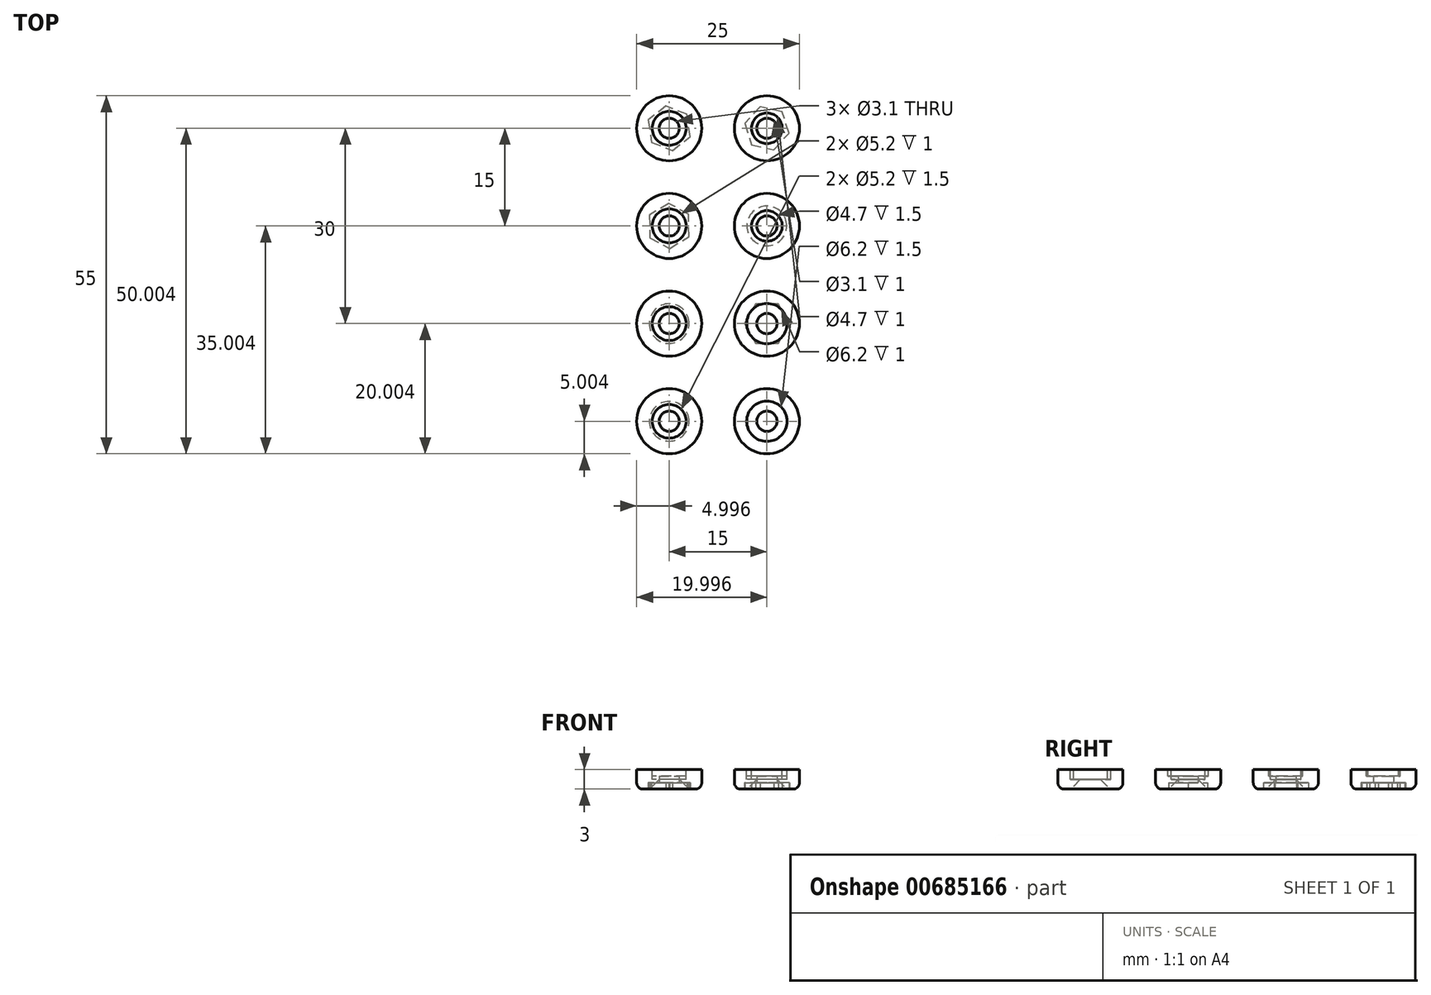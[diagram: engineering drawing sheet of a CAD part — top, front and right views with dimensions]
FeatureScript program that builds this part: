
annotation { "Feature Type Name" : "Feature", "Feature Type Description" : "" }
export const myFeature = defineFeature(function(context is Context, id is Id, definition is map)
    precondition{}
    {
        {
            var Q0;
            Q0=qCreatedBy(makeId("Top.planeOp"),FACE);
            var sketch = newSketch(context, id + "F0", { "sketchPlane" : qUnion([Q0])});
            skCircle(sketch, "E0", {"center": v(-31.01, -17.67) * mm, "radius": 5 * mm});
            skCircle(sketch, "E1.0.1.0", {"center": v(-31.01, -2.67) * mm, "radius": 5 * mm});
            skCircle(sketch, "E1.0.2.0", {"center": v(-31.01, 12.33) * mm, "radius": 5 * mm});
            skCircle(sketch, "E1.0.3.0", {"center": v(-31.01, 27.33) * mm, "radius": 5 * mm});
            skCircle(sketch, "E1.1.0.0", {"center": v(-16.01, -17.67) * mm, "radius": 5 * mm});
            skCircle(sketch, "E1.1.1.0", {"center": v(-16.01, -2.67) * mm, "radius": 5 * mm});
            skCircle(sketch, "E1.1.2.0", {"center": v(-16.01, 12.33) * mm, "radius": 5 * mm});
            skCircle(sketch, "E1.1.3.0", {"center": v(-16.01, 27.33) * mm, "radius": 5 * mm});
            skLineSegment(sketch, "E1.direction1", {"start": v(-31.01, -17.67) * mm, "end": v(-16.01, -17.67) * mm, "construction": true});
            skLineSegment(sketch, "E1.direction2", {"start": v(-31.01, -17.67) * mm, "end": v(-31.01, -2.67) * mm, "construction": true});
            skCircle(sketch, "E2", {"center": v(-31.01, -17.67) * mm, "radius": 1.55 * mm});
            skCircle(sketch, "E3", {"center": v(-16.01, -17.67) * mm, "radius": 1.55 * mm});
            skCircle(sketch, "E4", {"center": v(-31.01, -2.67) * mm, "radius": 1.55 * mm});
            skCircle(sketch, "E5", {"center": v(-16.01, -2.67) * mm, "radius": 1.55 * mm});
            skCircle(sketch, "E6", {"center": v(-31.01, 12.33) * mm, "radius": 1.55 * mm});
            skCircle(sketch, "E7", {"center": v(-31.01, 27.33) * mm, "radius": 1.55 * mm});
            skCircle(sketch, "E8", {"center": v(-16.01, 12.33) * mm, "radius": 1.55 * mm});
            skCircle(sketch, "E9", {"center": v(-16.01, 27.33) * mm, "radius": 1.55 * mm});
            skSolve(sketch);
        }
        {
            var Q0;
            Q0 = qSketchRegion(id + "F0", true);
            extrude(context, id + "F1", {"entities" : qUnion([Q0]), "depth" : 3 * mm, "offsetDistance" : 25 * mm});
        }
        {
            var Q0;
            Q0=makeQuery(id+"F1.opExtrude","CAP_FACE",FACE,{"disambiguationData":[OSD([sQuery(id+"F0.wireOp",EDGE,"E0")])],"isStart":false});
            var sketch = newSketch(context, id + "F2", { "sketchPlane" : qUnion([Q0])});
            skCircle(sketch, "E10", {"center": v(-31.01, -17.67) * mm, "radius": 2.6 * mm});
            skSolve(sketch);
        }
        {
            var Q0;
            Q0 = qSketchRegion(id + "F2", true);
            extrude(context, id + "F3", {"entities" : qUnion([Q0]), "operationType" : NewBodyOperationType.REMOVE, "oppositeDirection" : true, "depth" : 1.5 * mm, "offsetDistance" : 25 * mm});
        }
        {
            var Q0;
            Q0=makeQuery(id+"F1.opExtrude","CAP_FACE",FACE,{"disambiguationData":[OSD([sQuery(id+"F0.wireOp",EDGE,"E1.0.1.0")])],"isStart":false});
            var sketch = newSketch(context, id + "F4", { "sketchPlane" : qUnion([Q0])});
            skCircle(sketch, "E11", {"center": v(-31.01, -2.67) * mm, "radius": 2.6 * mm});
            skSolve(sketch);
        }
        {
            var Q0;
            Q0 = qSketchRegion(id + "F4", true);
            extrude(context, id + "F5", {"entities" : qUnion([Q0]), "operationType" : NewBodyOperationType.REMOVE, "oppositeDirection" : true, "depth" : 1.5 * mm, "offsetDistance" : 25 * mm});
        }
        {
            var Q0;
            Q0=makeQuery(id+"F1.opExtrude","CAP_FACE",FACE,{"disambiguationData":[OSD([sQuery(id+"F0.wireOp",EDGE,"E1.0.2.0")])],"isStart":false});
            var sketch = newSketch(context, id + "F6", { "sketchPlane" : qUnion([Q0])});
            skCircle(sketch, "E12", {"center": v(-31.01, 12.33) * mm, "radius": 2.6 * mm});
            skSolve(sketch);
        }
        {
            var Q0;
            Q0 = qSketchRegion(id + "F6", true);
            extrude(context, id + "F7", {"entities" : qUnion([Q0]), "operationType" : NewBodyOperationType.REMOVE, "oppositeDirection" : true, "depth" : 1 * mm, "offsetDistance" : 25 * mm});
        }
        {
            var Q0;
            Q0=makeQuery(id+"F1.opExtrude","CAP_FACE",FACE,{"disambiguationData":[OSD([sQuery(id+"F0.wireOp",EDGE,"E1.0.3.0")])],"isStart":false});
            var sketch = newSketch(context, id + "F8", { "sketchPlane" : qUnion([Q0])});
            skCircle(sketch, "E13", {"center": v(-31.01, 27.33) * mm, "radius": 2.6 * mm});
            skSolve(sketch);
        }
        {
            var Q0;
            Q0 = qSketchRegion(id + "F8", true);
            extrude(context, id + "F9", {"entities" : qUnion([Q0]), "operationType" : NewBodyOperationType.REMOVE, "oppositeDirection" : true, "depth" : 1 * mm, "offsetDistance" : 25 * mm});
        }
        {
            var Q0;
            Q0=makeQuery(id+"F1.opExtrude","CAP_FACE",FACE,{"disambiguationData":[OSD([sQuery(id+"F0.wireOp",EDGE,"E1.1.0.0")])],"isStart":false});
            var sketch = newSketch(context, id + "F10", { "sketchPlane" : qUnion([Q0])});
            skCircle(sketch, "E14", {"center": v(-16.01, -17.67) * mm, "radius": 3.1 * mm});
            skSolve(sketch);
        }
        {
            var Q0;
            Q0 = qSketchRegion(id + "F10", true);
            extrude(context, id + "F11", {"entities" : qUnion([Q0]), "operationType" : NewBodyOperationType.REMOVE, "oppositeDirection" : true, "depth" : 1.5 * mm, "offsetDistance" : 25 * mm});
        }
        {
            var Q0;
            Q0=makeQuery(id+"F1.opExtrude","CAP_FACE",FACE,{"disambiguationData":[OSD([sQuery(id+"F0.wireOp",EDGE,"E1.1.1.0")])],"isStart":false});
            var sketch = newSketch(context, id + "F12", { "sketchPlane" : qUnion([Q0])});
            skCircle(sketch, "E15", {"center": v(-16.01, -2.67) * mm, "radius": 3.1 * mm});
            skSolve(sketch);
        }
        {
            var Q0;
            Q0 = qSketchRegion(id + "F12", true);
            extrude(context, id + "F13", {"entities" : qUnion([Q0]), "operationType" : NewBodyOperationType.REMOVE, "oppositeDirection" : true, "depth" : 1 * mm, "offsetDistance" : 25 * mm});
        }
        {
            var Q0;
            Q0=makeQuery(id+"F1.opExtrude","CAP_FACE",FACE,{"disambiguationData":[OSD([sQuery(id+"F0.wireOp",EDGE,"E1.1.2.0")])],"isStart":false});
            var sketch = newSketch(context, id + "F14", { "sketchPlane" : qUnion([Q0])});
            skCircle(sketch, "E16", {"center": v(-16.01, 12.33) * mm, "radius": 2.35 * mm});
            skSolve(sketch);
        }
        {
            var Q0;
            Q0 = qSketchRegion(id + "F14", true);
            extrude(context, id + "F15", {"entities" : qUnion([Q0]), "operationType" : NewBodyOperationType.REMOVE, "oppositeDirection" : true, "depth" : 1.5 * mm, "offsetDistance" : 25 * mm});
        }
        {
            var Q0;
            Q0=makeQuery(id+"F1.opExtrude","CAP_FACE",FACE,{"disambiguationData":[OSD([sQuery(id+"F0.wireOp",EDGE,"E1.1.3.0")])],"isStart":false});
            var sketch = newSketch(context, id + "F16", { "sketchPlane" : qUnion([Q0])});
            skCircle(sketch, "E17", {"center": v(-16.01, 27.33) * mm, "radius": 2.35 * mm});
            skSolve(sketch);
        }
        {
            var Q0;
            Q0 = qSketchRegion(id + "F16", true);
            extrude(context, id + "F17", {"entities" : qUnion([Q0]), "operationType" : NewBodyOperationType.REMOVE, "oppositeDirection" : true, "depth" : 1 * mm, "offsetDistance" : 25 * mm});
        }
        {
            var Q0;
            Q0=makeQuery(id+"F1.opExtrude","CAP_FACE",FACE,{"disambiguationData":[OSD([sQuery(id+"F0.wireOp",EDGE,"E1.0.3.0")])],"isStart":true});
            var sketch = newSketch(context, id + "F18", { "sketchPlane" : qUnion([Q0])});
            skCircle(sketch, "E18.cCircle", {"center": v(-31.01, -27.33) * mm, "radius": 3 * mm, "construction": true});
            skLineSegment(sketch, "E18.0", {"start": v(-28.29, -29.47) * mm, "end": v(-31.5, -30.76) * mm});
            skLineSegment(sketch, "E18.1", {"start": v(-31.5, -30.76) * mm, "end": v(-34.23, -28.62) * mm});
            skLineSegment(sketch, "E18.2", {"start": v(-34.23, -28.62) * mm, "end": v(-33.74, -25.2) * mm});
            skLineSegment(sketch, "E18.3", {"start": v(-33.74, -25.2) * mm, "end": v(-30.52, -23.9) * mm});
            skLineSegment(sketch, "E18.4", {"start": v(-30.52, -23.9) * mm, "end": v(-27.8, -26.04) * mm});
            skLineSegment(sketch, "E18.5", {"start": v(-27.8, -26.04) * mm, "end": v(-28.29, -29.47) * mm});
            skPoint(sketch, "E18.0.midPoint", {"position": v(-29.9, -30.12) * mm});
            skSolve(sketch);
        }
        {
            var Q0;
            Q0 = qSketchRegion(id + "F18", true);
            extrude(context, id + "F19", {"entities" : qUnion([Q0]), "operationType" : NewBodyOperationType.REMOVE, "oppositeDirection" : true, "depth" : 1 * mm, "offsetDistance" : 25 * mm});
        }
        {
            var Q0;
            Q0=makeQuery(id+"F1.opExtrude","CAP_FACE",FACE,{"disambiguationData":[OSD([sQuery(id+"F0.wireOp",EDGE,"E1.0.2.0")])],"isStart":true});
            var sketch = newSketch(context, id + "F20", { "sketchPlane" : qUnion([Q0])});
            skCircle(sketch, "E19.cCircle", {"center": v(-31.01, -12.33) * mm, "radius": 3 * mm, "construction": true});
            skLineSegment(sketch, "E19.0", {"start": v(-28.05, -14.13) * mm, "end": v(-31.1, -15.8) * mm});
            skLineSegment(sketch, "E19.1", {"start": v(-31.1, -15.8) * mm, "end": v(-34.05, -14) * mm});
            skLineSegment(sketch, "E19.2", {"start": v(-34.05, -14) * mm, "end": v(-33.97, -10.53) * mm});
            skLineSegment(sketch, "E19.3", {"start": v(-33.97, -10.53) * mm, "end": v(-30.93, -8.87) * mm});
            skLineSegment(sketch, "E19.4", {"start": v(-30.93, -8.87) * mm, "end": v(-27.98, -10.67) * mm});
            skLineSegment(sketch, "E19.5", {"start": v(-27.98, -10.67) * mm, "end": v(-28.05, -14.13) * mm});
            skPoint(sketch, "E19.0.midPoint", {"position": v(-29.57, -14.97) * mm});
            skSolve(sketch);
        }
        {
            var Q0;
            Q0 = qSketchRegion(id + "F20", true);
            extrude(context, id + "F21", {"entities" : qUnion([Q0]), "operationType" : NewBodyOperationType.REMOVE, "oppositeDirection" : true, "depth" : 1 * mm, "offsetDistance" : 25 * mm});
        }
        {
            var Q0;
            Q0=makeQuery(id+"F1.opExtrude","CAP_FACE",FACE,{"disambiguationData":[OSD([sQuery(id+"F0.wireOp",EDGE,"E1.1.3.0")])],"isStart":true});
            var sketch = newSketch(context, id + "F22", { "sketchPlane" : qUnion([Q0])});
            skCircle(sketch, "E20.cCircle", {"center": v(-16.01, -27.33) * mm, "radius": 3 * mm, "construction": true});
            skLineSegment(sketch, "E20.0", {"start": v(-13.67, -29.88) * mm, "end": v(-17.05, -30.64) * mm});
            skLineSegment(sketch, "E20.1", {"start": v(-17.05, -30.64) * mm, "end": v(-19.4, -28.1) * mm});
            skLineSegment(sketch, "E20.2", {"start": v(-19.4, -28.1) * mm, "end": v(-18.36, -24.79) * mm});
            skLineSegment(sketch, "E20.3", {"start": v(-18.36, -24.79) * mm, "end": v(-14.98, -24.03) * mm});
            skLineSegment(sketch, "E20.4", {"start": v(-14.98, -24.03) * mm, "end": v(-12.63, -26.57) * mm});
            skLineSegment(sketch, "E20.5", {"start": v(-12.63, -26.57) * mm, "end": v(-13.67, -29.88) * mm});
            skPoint(sketch, "E20.0.midPoint", {"position": v(-15.36, -30.26) * mm});
            skSolve(sketch);
        }
        {
            var Q0;
            Q0 = qSketchRegion(id + "F22", true);
            extrude(context, id + "F23", {"entities" : qUnion([Q0]), "operationType" : NewBodyOperationType.REMOVE, "oppositeDirection" : true, "depth" : 1 * mm, "offsetDistance" : 25 * mm});
        }
        {
            var Q0;
            Q0=makeQuery(id+"F1.opExtrude","CAP_FACE",FACE,{"disambiguationData":[OSD([sQuery(id+"F0.wireOp",EDGE,"E1.1.1.0")])],"isStart":true});
            var sketch = newSketch(context, id + "F24", { "sketchPlane" : qUnion([Q0])});
            skCircle(sketch, "E21.cCircle", {"center": v(-16.01, 2.67) * mm, "radius": 3 * mm, "construction": true});
            skLineSegment(sketch, "E21.0", {"start": v(-14.28, -0.33) * mm, "end": v(-17.75, -0.33) * mm});
            skLineSegment(sketch, "E21.1", {"start": v(-17.75, -0.33) * mm, "end": v(-19.48, 2.67) * mm});
            skLineSegment(sketch, "E21.2", {"start": v(-19.48, 2.67) * mm, "end": v(-17.75, 5.67) * mm});
            skLineSegment(sketch, "E21.3", {"start": v(-17.75, 5.67) * mm, "end": v(-14.28, 5.67) * mm});
            skLineSegment(sketch, "E21.4", {"start": v(-14.28, 5.67) * mm, "end": v(-12.55, 2.67) * mm});
            skLineSegment(sketch, "E21.5", {"start": v(-12.55, 2.67) * mm, "end": v(-14.28, -0.33) * mm});
            skPoint(sketch, "E21.0.midPoint", {"position": v(-16.01, -0.33) * mm});
            skSolve(sketch);
        }
        {
            var Q0;
            Q0 = qSketchRegion(id + "F24", true);
            extrude(context, id + "F25", {"entities" : qUnion([Q0]), "operationType" : NewBodyOperationType.REMOVE, "oppositeDirection" : true, "depth" : 1 * mm, "offsetDistance" : 25 * mm});
        }
        {
            var Q0;
            Q0=makeQuery(id+"F1.opExtrude","CAP_EDGE",EDGE,{"disambiguationData":[OSD([sQuery(id+"F0.wireOp",EDGE,"E3")])],"isStart":true});
            var Q1;
            Q1=makeQuery(id+"F1.opExtrude","CAP_EDGE",EDGE,{"disambiguationData":[OSD([sQuery(id+"F0.wireOp",EDGE,"E8")])],"isStart":true});
            var Q2;
            Q2=makeQuery(id+"F1.opExtrude","CAP_EDGE",EDGE,{"disambiguationData":[OSD([sQuery(id+"F0.wireOp",EDGE,"E4")])],"isStart":true});
            var Q3;
            Q3=makeQuery(id+"F1.opExtrude","CAP_EDGE",EDGE,{"disambiguationData":[OSD([sQuery(id+"F0.wireOp",EDGE,"E2")])],"isStart":true});
            chamfer(context, id + "F26", {"entities" : qUnion([Q0, Q1, Q2, Q3]), "width" : 1.5 * mm, "tangentPropagation" : true});
        }
        {
            var Q0;
            Q0=makeQuery(id+"F1.opExtrude","CAP_EDGE",EDGE,{"disambiguationData":[OSD([sQuery(id+"F0.wireOp",EDGE,"E0")])],"isStart":true});
            var Q1;
            Q1=makeQuery(id+"F1.opExtrude","CAP_EDGE",EDGE,{"disambiguationData":[OSD([sQuery(id+"F0.wireOp",EDGE,"E1.0.1.0")])],"isStart":true});
            var Q2;
            Q2=makeQuery(id+"F1.opExtrude","CAP_EDGE",EDGE,{"disambiguationData":[OSD([sQuery(id+"F0.wireOp",EDGE,"E1.1.1.0")])],"isStart":true});
            var Q3;
            Q3=makeQuery(id+"F1.opExtrude","CAP_EDGE",EDGE,{"disambiguationData":[OSD([sQuery(id+"F0.wireOp",EDGE,"E1.1.0.0")])],"isStart":true});
            var Q4;
            Q4=makeQuery(id+"F1.opExtrude","CAP_EDGE",EDGE,{"disambiguationData":[OSD([sQuery(id+"F0.wireOp",EDGE,"E1.1.2.0")])],"isStart":true});
            var Q5;
            Q5=makeQuery(id+"F1.opExtrude","CAP_EDGE",EDGE,{"disambiguationData":[OSD([sQuery(id+"F0.wireOp",EDGE,"E1.0.2.0")])],"isStart":true});
            var Q6;
            Q6=makeQuery(id+"F1.opExtrude","CAP_EDGE",EDGE,{"disambiguationData":[OSD([sQuery(id+"F0.wireOp",EDGE,"E1.0.3.0")])],"isStart":true});
            var Q7;
            Q7=makeQuery(id+"F1.opExtrude","CAP_EDGE",EDGE,{"disambiguationData":[OSD([sQuery(id+"F0.wireOp",EDGE,"E1.1.3.0")])],"isStart":true});
            fillet(context, id + "F27", {"entities" : qUnion([Q0, Q1, Q2, Q3, Q4, Q5, Q6, Q7]), "radius" : 1 * mm, "tangentPropagation" : true, "allowEdgeOverflow" : false});
        }
    });
